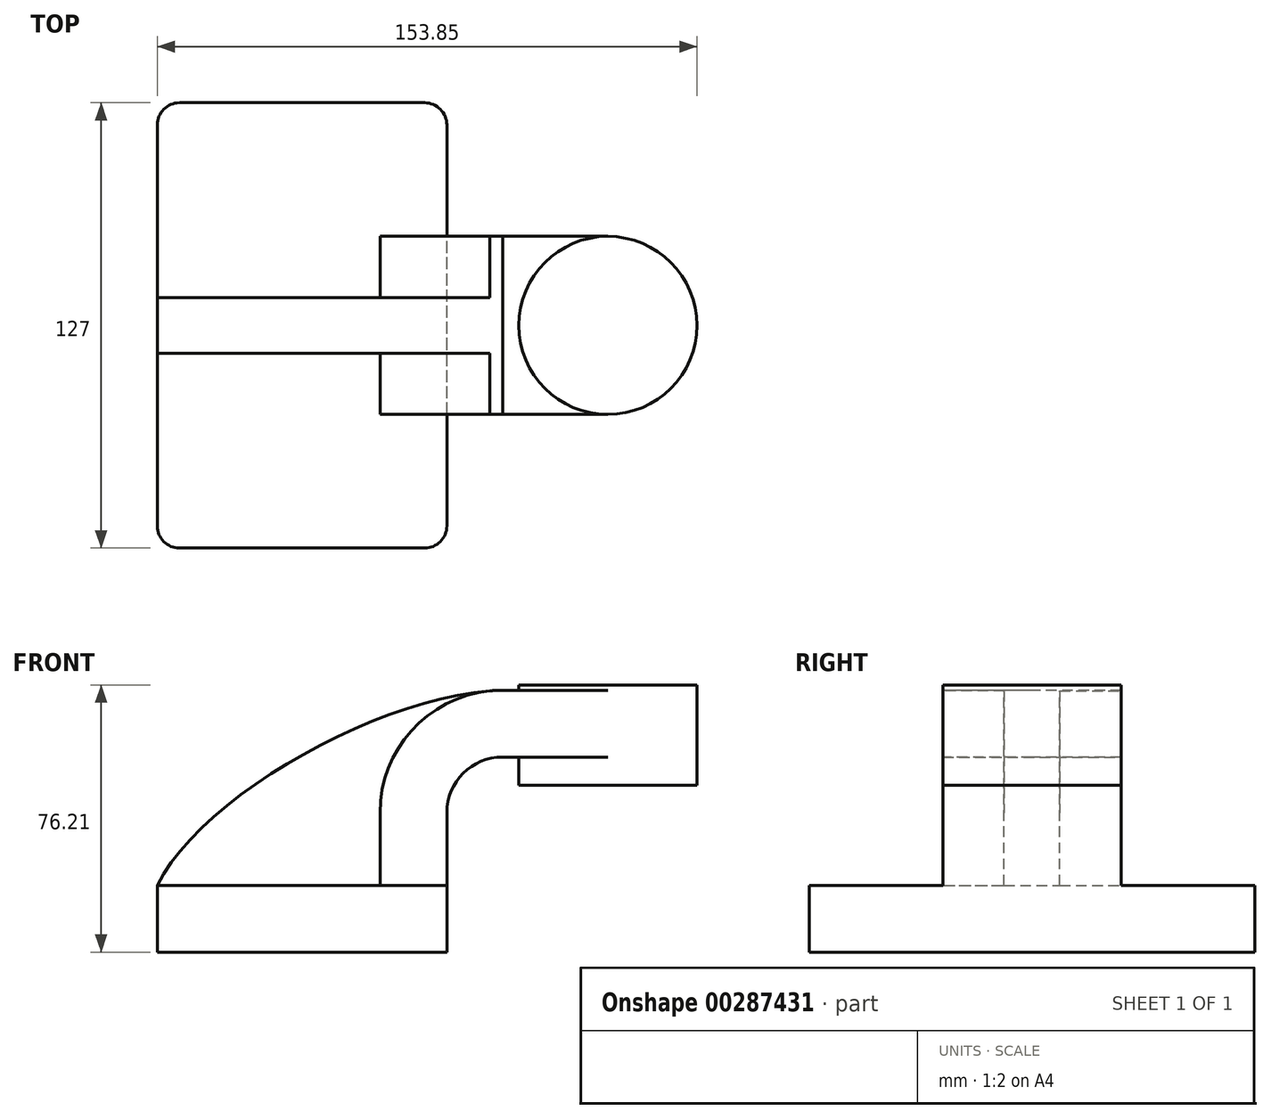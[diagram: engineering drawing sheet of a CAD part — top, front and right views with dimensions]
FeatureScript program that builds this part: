
annotation { "Feature Type Name" : "Feature", "Feature Type Description" : "" }
export const myFeature = defineFeature(function(context is Context, id is Id, definition is map)
    precondition{}
    {
        {
            var Q0;
            Q0=qCreatedBy(makeId("Front.planeOp"),FACE);
            var sketch = newSketch(context, id + "F0", { "sketchPlane" : qUnion([Q0])});
            skLineSegment(sketch, "E0.bottom", {"start": v(-41.27, -9.53) * mm, "end": v(41.28, -9.53) * mm});
            skLineSegment(sketch, "E0.top", {"start": v(-41.28, 9.52) * mm, "end": v(41.28, 9.52) * mm});
            skLineSegment(sketch, "E0.left", {"start": v(-41.28, -9.53) * mm, "end": v(-41.28, 9.53) * mm});
            skLineSegment(sketch, "E0.right", {"start": v(41.28, -9.53) * mm, "end": v(41.28, 9.52) * mm});
            skPoint(sketch, "E0.middle", {"position": v(0, 0) * mm});
            skLineSegment(sketch, "E1.bottom", {"start": v(61.77, 38.1) * mm, "end": v(112.57, 38.1) * mm});
            skLineSegment(sketch, "E1.top", {"start": v(61.77, 66.67) * mm, "end": v(112.57, 66.67) * mm});
            skLineSegment(sketch, "E1.left", {"start": v(61.77, 38.1) * mm, "end": v(61.77, 66.67) * mm});
            skLineSegment(sketch, "E1.right", {"start": v(112.57, 38.1) * mm, "end": v(112.57, 66.67) * mm});
            skPoint(sketch, "E1.middle", {"position": v(87.17, 52.39) * mm});
            skLineSegment(sketch, "E2", {"start": v(41.28, 9.52) * mm, "end": v(41.28, 30.23) * mm});
            skArc(sketch, "E3", {"start": v(41.27, 30.23) * mm, "mid": v(45.92, 41.46) * mm, "end": v(57.15, 46.1) * mm});
            skLineSegment(sketch, "E4", {"start": v(57.15, 46.1) * mm, "end": v(87.17, 46.1) * mm});
            skPoint(sketch, "E4.endSnap0", {"position": v(87.17, 38.1) * mm});
            skLineSegment(sketch, "E5.0", {"start": v(22.22, 9.52) * mm, "end": v(22.22, 30.23) * mm});
            skArc(sketch, "E6.0", {"start": v(22.23, 30.23) * mm, "mid": v(32.45, 54.93) * mm, "end": v(57.15, 65.16) * mm});
            skLineSegment(sketch, "E7.0", {"start": v(57.15, 65.16) * mm, "end": v(87.17, 65.16) * mm});
            skLineSegment(sketch, "E8", {"start": v(87.17, 38.1) * mm, "end": v(87.17, 66.67) * mm});
            skFitSpline(sketch, "E9", {"points": [v(-41.27, 9.52) * mm, v(57.15, 65.16) * mm], "startDerivative": vector(37.7, 76.99) * mm, "endDerivative": vector(100.61, 2.4) * mm});
            skSolve(sketch);
        }
        {
            var Q0;
            Q0=makeQuery(id+"F0.imprint","IMPRINT",FACE,{"disambiguationData":[TD([[makeQuery(id+"F0.imprint","IMPRINT",EDGE,{"derivedFrom":sQuery(id+"F0.wireOp",EDGE,"E0.bottom")}),1.0]])]});
            extrude(context, id + "F1", {"entities" : qUnion([Q0]), "endBound" : BoundingType.SYMMETRIC, "depth" : 127 * mm});
        }
        {
            var Q0;
            {var subQ1=sQuery(id+"F0.wireOp",EDGE,"E2");Q0=makeQuery(id+"F0.imprint","IMPRINT",FACE,{"disambiguationData":[TD([[makeQuery(id+"F0.imprint","IMPRINT",EDGE,{"derivedFrom":subQ1}),1.0]])]});}
            var Q1;
            {var subQ0=sQuery(id+"F0.wireOp",EDGE,"E4");var subQ1=sQuery(id+"F0.wireOp",EDGE,"E1.left");var subQ2=makeQuery(id+"F0.imprint","INTERSECT",VERTEX,{"derivedFrom":[subQ1,subQ0]});Q1=makeQuery(id+"F0.imprint","IMPRINT",FACE,{"disambiguationData":[TD([[makeQuery(id+"F0.imprint","IMPRINT",EDGE,{"disambiguationData":[TD([[subQ2,-1.0]])],"derivedFrom":subQ1}),-1.0]])]});}
            extrude(context, id + "F2", {"entities" : qUnion([Q0, Q1]), "operationType" : NewBodyOperationType.ADD, "endBound" : BoundingType.SYMMETRIC, "depth" : 50.8 * mm});
        }
        {
            var Q0;
            {var subQ3=sQuery(id+"F0.wireOp",EDGE,"E5.0");Q0=makeQuery(id+"F0.imprint","IMPRINT",FACE,{"disambiguationData":[TD([[makeQuery(id+"F0.imprint","IMPRINT",EDGE,{"derivedFrom":subQ3}),1.0]])]});}
            extrude(context, id + "F3", {"entities" : qUnion([Q0]), "operationType" : NewBodyOperationType.ADD, "endBound" : BoundingType.SYMMETRIC, "depth" : 15.88 * mm});
        }
        {
            var Q0;
            {var subQ4=sQuery(id+"F0.wireOp",EDGE,"E1.right");Q0=makeQuery(id+"F0.imprint","IMPRINT",FACE,{"disambiguationData":[TD([[makeQuery(id+"F0.imprint","IMPRINT",EDGE,{"derivedFrom":subQ4}),1.0]])]});}
            var Q1;
            Q1=sQuery(id+"F0.wireOp",EDGE,"E8");
            revolve(context, id + "F4", {"operationType" : NewBodyOperationType.ADD, "entities" : qUnion([Q0]), "axis" : qUnion([Q1]), "revolveType" : RevolveType.FULL});
        }
        {
            var Q0;
            Q0=makeQuery(id+"F1.opExtrude","CAP_EDGE",EDGE,{"disambiguationData":[OSD([sQuery(id+"F0.wireOp",EDGE,"E0.left")])],"isStart":false});
            var Q1;
            Q1=makeQuery(id+"F1.opExtrude","CAP_EDGE",EDGE,{"disambiguationData":[OSD([sQuery(id+"F0.wireOp",EDGE,"E0.right")])],"isStart":false});
            var Q2;
            Q2=makeQuery(id+"F1.opExtrude","CAP_EDGE",EDGE,{"disambiguationData":[OSD([sQuery(id+"F0.wireOp",EDGE,"E0.left")])],"isStart":true});
            var Q3;
            Q3=makeQuery(id+"F1.opExtrude","CAP_EDGE",EDGE,{"disambiguationData":[OSD([sQuery(id+"F0.wireOp",EDGE,"E0.right")])],"isStart":true});
            fillet(context, id + "F5", {"entities" : qUnion([Q0, Q1, Q2, Q3]), "radius" : 6.35 * mm, "tangentPropagation" : true, "allowEdgeOverflow" : false});
        }
    });
